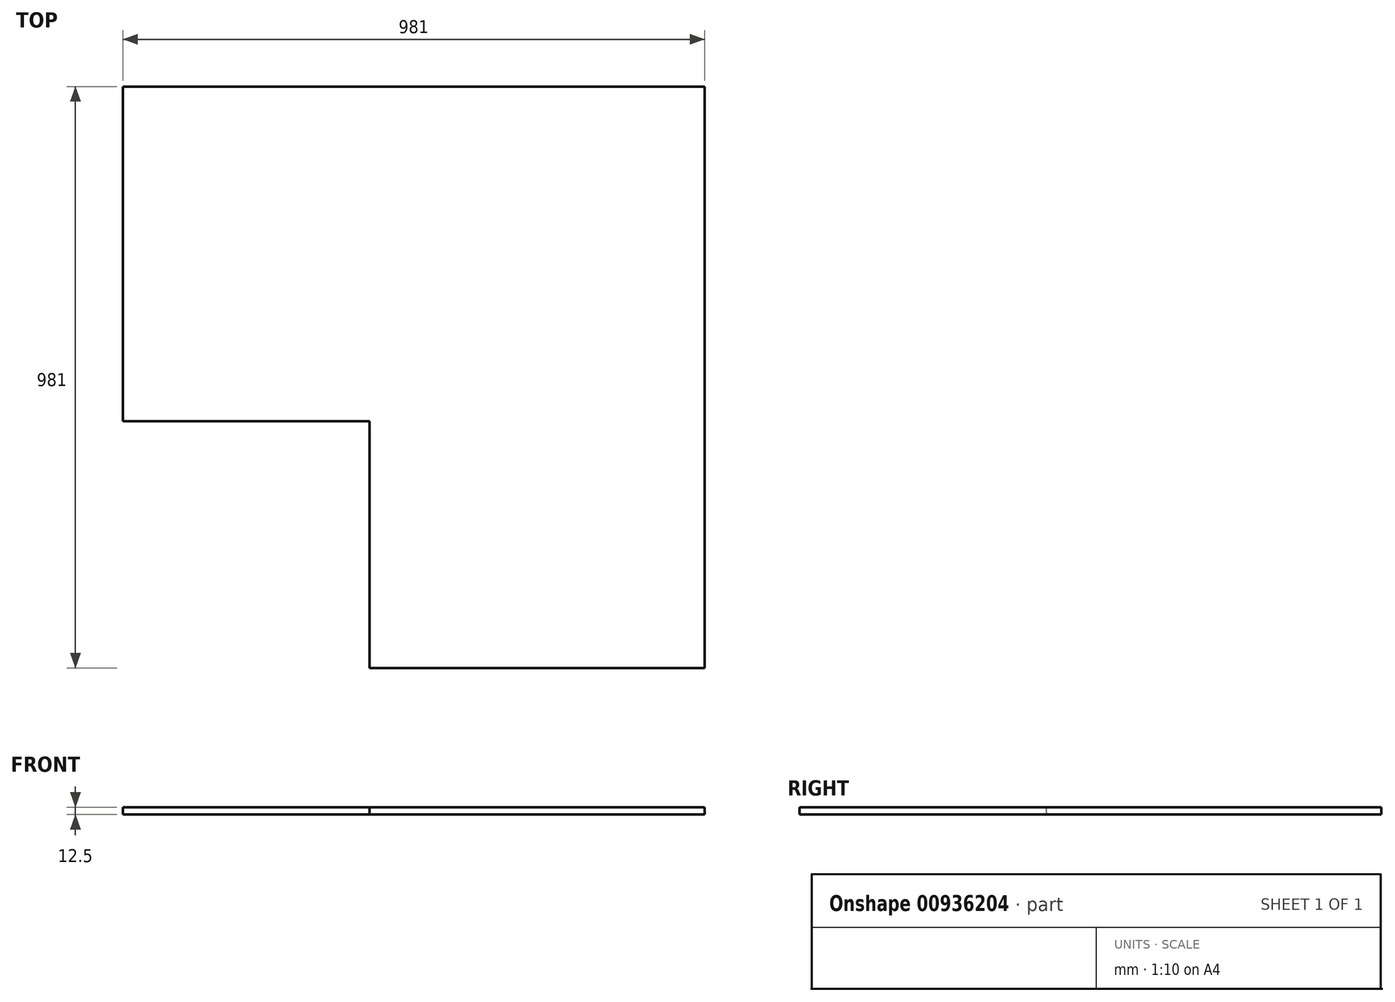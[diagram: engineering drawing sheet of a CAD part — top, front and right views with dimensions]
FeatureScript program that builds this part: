
annotation { "Feature Type Name" : "Feature", "Feature Type Description" : "" }
export const myFeature = defineFeature(function(context is Context, id is Id, definition is map)
    precondition{}
    {
        {
            var Q0;
            Q0=qCreatedBy(makeId("Top.planeOp"),FACE);
            var sketch = newSketch(context, id + "F0", { "sketchPlane" : qUnion([Q0])});
            skLineSegment(sketch, "E0.bottom", {"start": v(416, 0) * mm, "end": v(981, 0) * mm});
            skLineSegment(sketch, "E0.top", {"start": v(0, 981) * mm, "end": v(981, 981) * mm});
            skLineSegment(sketch, "E0.left", {"start": v(0, 416) * mm, "end": v(0, 981) * mm});
            skLineSegment(sketch, "E0.right", {"start": v(981, 0) * mm, "end": v(981, 981) * mm});
            skLineSegment(sketch, "E1", {"start": v(0, 416) * mm, "end": v(416, 416) * mm});
            skLineSegment(sketch, "E2", {"start": v(416, 416) * mm, "end": v(416, 0) * mm});
            skSolve(sketch);
        }
        {
            var Q0;
            Q0 = qSketchRegion(id + "F0", true);
            extrude(context, id + "F1", {"entities" : qUnion([Q0]), "depth" : 12.5 * mm, "offsetDistance" : 25 * mm});
        }
    });
